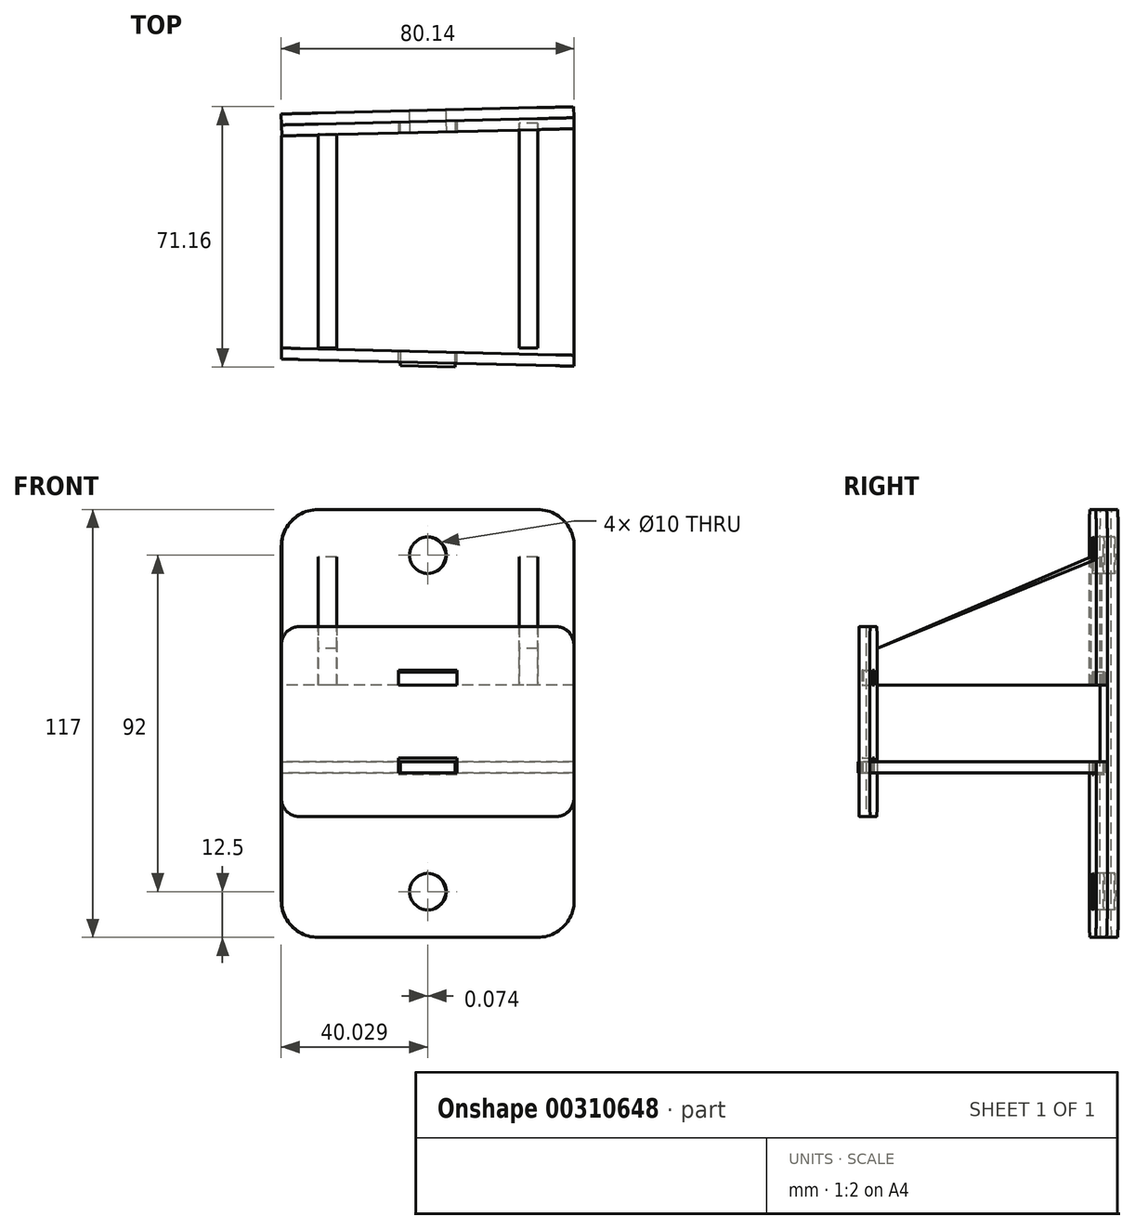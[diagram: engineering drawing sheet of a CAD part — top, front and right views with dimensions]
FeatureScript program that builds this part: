
annotation { "Feature Type Name" : "Feature", "Feature Type Description" : "" }
export const myFeature = defineFeature(function(context is Context, id is Id, definition is map)
    precondition{}
    {
        {
            var Q0;
            Q0=qCreatedBy(makeId("Top.planeOp"),FACE);
            var sketch = newSketch(context, id + "F0", { "sketchPlane" : qUnion([Q0])});
            skLineSegment(sketch, "E0", {"start": v(0, 58) * mm, "end": v(0, 0) * mm});
            skLineSegment(sketch, "E1", {"start": v(0, 0) * mm, "end": v(32.5, -0.8) * mm});
            skLineSegment(sketch, "E2", {"start": v(80, -1.98) * mm, "end": v(80, 59.98) * mm});
            skLineSegment(sketch, "E3", {"start": v(80, 59.98) * mm, "end": v(47.5, 59.18) * mm});
            skLineSegment(sketch, "E4", {"start": v(32.5, -0.8) * mm, "end": v(32.4, -4.8) * mm});
            skLineSegment(sketch, "E5", {"start": v(32.4, -4.8) * mm, "end": v(47.4, -5.18) * mm});
            skLineSegment(sketch, "E6", {"start": v(47.4, -5.18) * mm, "end": v(47.5, -1.18) * mm});
            skLineSegment(sketch, "E7", {"start": v(32.5, 58.8) * mm, "end": v(32.43, 61.8) * mm});
            skLineSegment(sketch, "E8", {"start": v(32.43, 61.8) * mm, "end": v(47.42, 62.18) * mm});
            skLineSegment(sketch, "E9", {"start": v(47.42, 62.18) * mm, "end": v(47.5, 59.18) * mm});
            skLineSegment(sketch, "E10.trimOffspring", {"start": v(32.5, 58.8) * mm, "end": v(0, 58) * mm});
            skLineSegment(sketch, "E11.trimOffspring", {"start": v(47.5, -1.18) * mm, "end": v(80, -1.98) * mm});
            skSolve(sketch);
        }
        {
            var Q0;
            Q0 = qSketchRegion(id + "F0", true);
            extrude(context, id + "F1", {"entities" : qUnion([Q0]), "depth" : 3 * mm});
        }
        {
            var Q0;
            Q0=makeQuery(id+"F1.opExtrude","SWEPT_FACE",FACE,{"disambiguationData":[OSD([sQuery(id+"F0.wireOp",EDGE,"E1")])]});
            var sketch = newSketch(context, id + "F2", { "sketchPlane" : qUnion([Q0])});
            skLineSegment(sketch, "E12.bottom", {"start": v(5, -12) * mm, "end": v(75, -12) * mm});
            skLineSegment(sketch, "E12.top", {"start": v(5, 40) * mm, "end": v(75, 40) * mm});
            skLineSegment(sketch, "E12.left", {"start": v(0, -7) * mm, "end": v(0, 35) * mm});
            skLineSegment(sketch, "E12.right", {"start": v(80, -7) * mm, "end": v(80, 35) * mm});
            skLineSegment(sketch, "E13.bottom", {"start": v(32, 0) * mm, "end": v(48, 0) * mm});
            skLineSegment(sketch, "E13.top", {"start": v(32, 4) * mm, "end": v(48, 4) * mm});
            skLineSegment(sketch, "E13.left", {"start": v(32, 0) * mm, "end": v(32, 4) * mm});
            skLineSegment(sketch, "E13.right", {"start": v(48, 0) * mm, "end": v(48, 4) * mm});
            skLineSegment(sketch, "E14.bottom", {"start": v(32, 28) * mm, "end": v(48, 28) * mm});
            skLineSegment(sketch, "E14.top", {"start": v(32, 24) * mm, "end": v(48, 24) * mm});
            skLineSegment(sketch, "E14.left", {"start": v(32, 28) * mm, "end": v(32, 24) * mm});
            skLineSegment(sketch, "E14.right", {"start": v(48, 28) * mm, "end": v(48, 24) * mm});
            skPoint(sketch, "E15.visualSharp", {"position": v(80, 40) * mm});
            skArc(sketch, "E15.filletArc", {"start": v(80, 35) * mm, "mid": v(78.54, 38.54) * mm, "end": v(75, 40) * mm});
            skPoint(sketch, "E16.visualSharp", {"position": v(0, 40) * mm});
            skArc(sketch, "E16.filletArc", {"start": v(5, 40) * mm, "mid": v(1.46, 38.54) * mm, "end": v(0, 35) * mm});
            skPoint(sketch, "E17.visualSharp", {"position": v(0, -12) * mm});
            skArc(sketch, "E17.filletArc", {"start": v(0, -7) * mm, "mid": v(1.46, -10.54) * mm, "end": v(5, -12) * mm});
            skPoint(sketch, "E18.visualSharp", {"position": v(80, -12) * mm});
            skArc(sketch, "E18.filletArc", {"start": v(75, -12) * mm, "mid": v(78.54, -10.54) * mm, "end": v(80, -7) * mm});
            skSolve(sketch);
        }
        {
            var Q0;
            Q0 = qSketchRegion(id + "F2", true);
            extrude(context, id + "F3", {"entities" : qUnion([Q0]), "depth" : 3 * mm});
        }
        {
            var Q0;
            Q0=makeQuery(id+"F1.opExtrude","SWEPT_FACE",FACE,{"disambiguationData":[OSD([sQuery(id+"F0.wireOp",EDGE,"E10.trimOffspring")])]});
            var sketch = newSketch(context, id + "F4", { "sketchPlane" : qUnion([Q0])});
            skLineSegment(sketch, "E19.bottom", {"start": v(-71.45, -45) * mm, "end": v(-11.45, -45) * mm});
            skLineSegment(sketch, "E19.top", {"start": v(-71.45, 72) * mm, "end": v(-11.45, 72) * mm});
            skLineSegment(sketch, "E19.left", {"start": v(-81.45, -35) * mm, "end": v(-81.45, 3) * mm});
            skLineSegment(sketch, "E19.right", {"start": v(-1.45, -35) * mm, "end": v(-1.45, 3) * mm});
            skLineSegment(sketch, "E20.bottom", {"start": v(-49.45, 27.5) * mm, "end": v(-33.45, 27.5) * mm});
            skLineSegment(sketch, "E20.top", {"start": v(-81.45, 24) * mm, "end": v(-49.45, 24) * mm});
            skLineSegment(sketch, "E20.left", {"start": v(-49.45, 27.5) * mm, "end": v(-49.45, 24) * mm});
            skLineSegment(sketch, "E20.right", {"start": v(-33.45, 27.5) * mm, "end": v(-33.45, 24) * mm});
            skLineSegment(sketch, "E21.bottom", {"start": v(-81.45, 3) * mm, "end": v(-49.45, 3) * mm});
            skLineSegment(sketch, "E21.top", {"start": v(-49.45, -0.5) * mm, "end": v(-33.45, -0.5) * mm});
            skLineSegment(sketch, "E21.left", {"start": v(-49.45, 3) * mm, "end": v(-49.45, -0.5) * mm});
            skLineSegment(sketch, "E21.right", {"start": v(-33.45, 3) * mm, "end": v(-33.45, -0.5) * mm});
            skLineSegment(sketch, "E22.trimOffspring", {"start": v(-33.45, 24) * mm, "end": v(-1.45, 24) * mm});
            skLineSegment(sketch, "E23.trimOffspring", {"start": v(-81.45, 24) * mm, "end": v(-81.45, 62) * mm});
            skLineSegment(sketch, "E24.trimOffspring", {"start": v(-1.45, 24) * mm, "end": v(-1.45, 62) * mm});
            skLineSegment(sketch, "E25.trimOffspring", {"start": v(-33.45, 3) * mm, "end": v(-1.45, 3) * mm});
            skCircle(sketch, "E26", {"center": v(-41.45, 59.5) * mm, "radius": 5 * mm});
            skCircle(sketch, "E27", {"center": v(-41.45, -32.5) * mm, "radius": 5 * mm});
            skPoint(sketch, "E28.visualSharp", {"position": v(-81.45, 72) * mm});
            skArc(sketch, "E28.filletArc", {"start": v(-71.45, 72) * mm, "mid": v(-78.52, 69.07) * mm, "end": v(-81.45, 62) * mm});
            skPoint(sketch, "E29.visualSharp", {"position": v(-1.45, 72) * mm});
            skArc(sketch, "E29.filletArc", {"start": v(-1.45, 62) * mm, "mid": v(-4.38, 69.07) * mm, "end": v(-11.45, 72) * mm});
            skPoint(sketch, "E30.visualSharp", {"position": v(-81.45, -45) * mm});
            skArc(sketch, "E30.filletArc", {"start": v(-81.45, -35) * mm, "mid": v(-78.52, -42.07) * mm, "end": v(-71.45, -45) * mm});
            skPoint(sketch, "E31.visualSharp", {"position": v(-1.45, -45) * mm});
            skArc(sketch, "E31.filletArc", {"start": v(-11.45, -45) * mm, "mid": v(-4.38, -42.07) * mm, "end": v(-1.45, -35) * mm});
            skSolve(sketch);
        }
        {
            var Q0;
            Q0 = qSketchRegion(id + "F4", true);
            extrude(context, id + "F5", {"entities" : qUnion([Q0]), "depth" : 3 * mm});
        }
        {
            var Q0;
            Q0=makeQuery(id+"F5.opExtrude","CAP_FACE",FACE,{"disambiguationData":[OSD([sQuery(id+"F4.wireOp",EDGE,"E19.top"),sQuery(id+"F4.wireOp",EDGE,"E20.bottom"),sQuery(id+"F4.wireOp",EDGE,"E20.top"),sQuery(id+"F4.wireOp",EDGE,"E20.left"),sQuery(id+"F4.wireOp",EDGE,"E20.right"),sQuery(id+"F4.wireOp",EDGE,"E22.trimOffspring"),sQuery(id+"F4.wireOp",EDGE,"E23.trimOffspring"),sQuery(id+"F4.wireOp",EDGE,"E24.trimOffspring"),sQuery(id+"F4.wireOp",EDGE,"E26")])],"isStart":false});
            var sketch = newSketch(context, id + "F6", { "sketchPlane" : qUnion([Q0])});
            skLineSegment(sketch, "E32.bottom", {"start": v(-71.45, -45) * mm, "end": v(-11.45, -45) * mm});
            skLineSegment(sketch, "E32.top", {"start": v(-71.45, 72) * mm, "end": v(-11.45, 72) * mm});
            skLineSegment(sketch, "E32.left", {"start": v(-81.45, -35) * mm, "end": v(-81.45, 62) * mm});
            skLineSegment(sketch, "E32.right", {"start": v(-1.45, -35) * mm, "end": v(-1.45, 62) * mm});
            skLineSegment(sketch, "E33.bottom", {"start": v(-81.45, 38.5) * mm, "end": v(-1.45, 38.5) * mm, "construction": true});
            skLineSegment(sketch, "E33.top", {"start": v(-81.45, -11.5) * mm, "end": v(-1.45, -11.5) * mm, "construction": true});
            skLineSegment(sketch, "E33.left", {"start": v(-81.45, 38.5) * mm, "end": v(-81.45, -11.5) * mm, "construction": true});
            skLineSegment(sketch, "E33.right", {"start": v(-1.45, 38.5) * mm, "end": v(-1.45, -11.5) * mm, "construction": true});
            skPoint(sketch, "E34", {"position": v(-41.45, 38.5) * mm});
            skPoint(sketch, "E35", {"position": v(-41.45, -11.5) * mm});
            skLineSegment(sketch, "E36", {"start": v(-41.45, 72) * mm, "end": v(-41.45, 38.5) * mm, "construction": true});
            skLineSegment(sketch, "E37", {"start": v(-41.45, -11.5) * mm, "end": v(-41.45, 38.5) * mm, "construction": true});
            skLineSegment(sketch, "E38", {"start": v(-41.45, -11.5) * mm, "end": v(-41.45, -45) * mm, "construction": true});
            skCircle(sketch, "E39", {"center": v(-41.45, -32.5) * mm, "radius": 5 * mm});
            skPoint(sketch, "E39.centerSnap0", {"position": v(-41.45, 72) * mm});
            skCircle(sketch, "E40", {"center": v(-41.45, 59.5) * mm, "radius": 5 * mm});
            skPoint(sketch, "E41.visualSharp", {"position": v(-81.45, 72) * mm});
            skArc(sketch, "E41.filletArc", {"start": v(-71.45, 72) * mm, "mid": v(-78.52, 69.07) * mm, "end": v(-81.45, 62) * mm});
            skPoint(sketch, "E42.visualSharp", {"position": v(-1.45, 72) * mm});
            skArc(sketch, "E42.filletArc", {"start": v(-1.45, 62) * mm, "mid": v(-4.38, 69.07) * mm, "end": v(-11.45, 72) * mm});
            skPoint(sketch, "E43.visualSharp", {"position": v(-1.45, -45) * mm});
            skArc(sketch, "E43.filletArc", {"start": v(-11.45, -45) * mm, "mid": v(-4.38, -42.07) * mm, "end": v(-1.45, -35) * mm});
            skPoint(sketch, "E44.visualSharp", {"position": v(-81.45, -45) * mm});
            skArc(sketch, "E44.filletArc", {"start": v(-81.45, -35) * mm, "mid": v(-78.52, -42.07) * mm, "end": v(-71.45, -45) * mm});
            skSolve(sketch);
        }
        {
            var Q0;
            Q0 = qSketchRegion(id + "F6", true);
            extrude(context, id + "F7", {"entities" : qUnion([Q0]), "depth" : 3 * mm});
        }
        {
            var Q0;
            Q0=qCreatedBy(makeId("Right.planeOp"),FACE);
            var sketch = newSketch(context, id + "F8", { "sketchPlane" : qUnion([Q0])});
            skLineSegment(sketch, "E45.top", {"start": v(58.5, 24) * mm, "end": v(0, 24) * mm});
            skLineSegment(sketch, "E45.left", {"start": v(58.5, 59) * mm, "end": v(58.5, 24) * mm});
            skLineSegment(sketch, "E46", {"start": v(0, 24) * mm, "end": v(0, 34) * mm});
            skLineSegment(sketch, "E47", {"start": v(0, 34) * mm, "end": v(58.5, 59) * mm});
            skSolve(sketch);
        }
        {
            var Q0;
            Q0 = qSketchRegion(id + "F8", true);
            extrude(context, id + "F9", {"entities" : qUnion([Q0]), "depth" : 5 * mm});
        }
        {
            var Q0;
            Q0=makeQuery(id+"F9.opExtrude","SWEPT_BODY",BODY,{"disambiguationData":[OSD([sQuery(id+"F8.wireOp",EDGE,"E45.top"),sQuery(id+"F8.wireOp",EDGE,"E45.left"),sQuery(id+"F8.wireOp",EDGE,"E46"),sQuery(id+"F8.wireOp",EDGE,"E47")])]});
            transform(context, id + "F10", {"entities" : qUnion([Q0]), "transformType" : TransformType.TRANSLATION_3D, "dx" : 10 * mm, "dy" : 0 * mm, "dz" : 0 * mm, "makeCopy" : false});
        }
        {
            var Q0;
            Q0=qCreatedBy(makeId("Right.planeOp"),FACE);
            var sketch = newSketch(context, id + "F11", { "sketchPlane" : qUnion([Q0])});
            skLineSegment(sketch, "E48", {"start": v(0, 24) * mm, "end": v(61.5, 24) * mm});
            skLineSegment(sketch, "E49", {"start": v(61.5, 24) * mm, "end": v(61.5, 59) * mm});
            skLineSegment(sketch, "E50", {"start": v(61.5, 59) * mm, "end": v(0, 34) * mm});
            skLineSegment(sketch, "E51", {"start": v(0, 34) * mm, "end": v(0, 24) * mm});
            skSolve(sketch);
        }
        {
            var Q0;
            Q0 = qSketchRegion(id + "F11", true);
            extrude(context, id + "F12", {"entities" : qUnion([Q0]), "depth" : 5 * mm});
        }
        {
            var Q0;
            Q0=makeQuery(id+"F12.opExtrude","SWEPT_BODY",BODY,{"disambiguationData":[OSD([sQuery(id+"F11.wireOp",EDGE,"E48"),sQuery(id+"F11.wireOp",EDGE,"E49"),sQuery(id+"F11.wireOp",EDGE,"E50"),sQuery(id+"F11.wireOp",EDGE,"E51")])]});
            transform(context, id + "F13", {"entities" : qUnion([Q0]), "transformType" : TransformType.TRANSLATION_3D, "dx" : 65 * mm, "dy" : 0 * mm, "dz" : 0 * mm, "makeCopy" : false});
        }
    });
